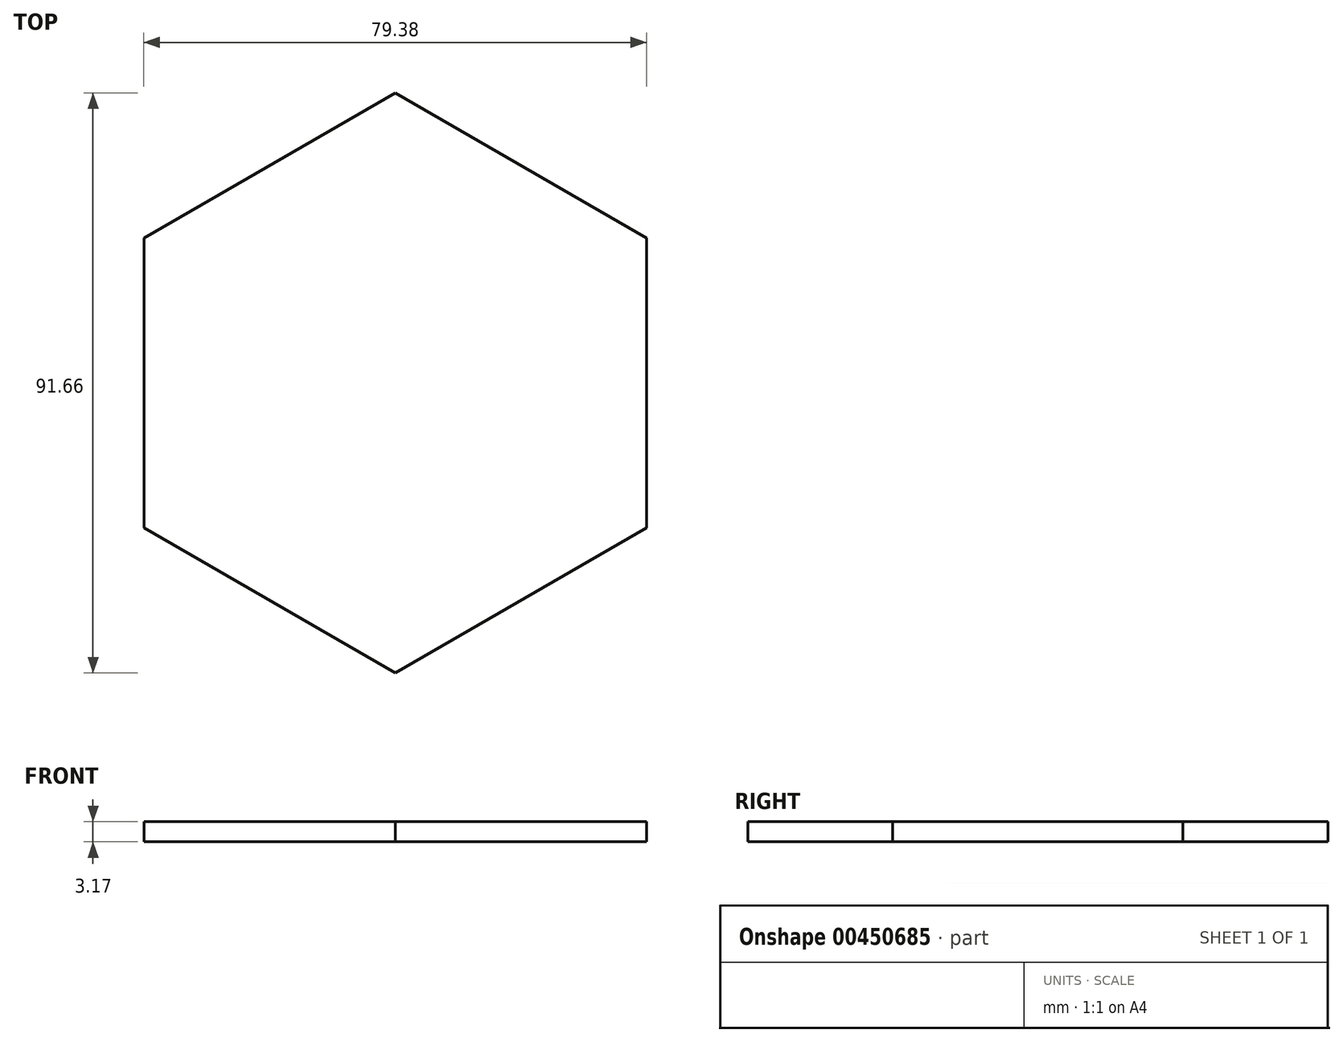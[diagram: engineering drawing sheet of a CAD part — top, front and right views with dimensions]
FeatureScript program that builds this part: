
annotation { "Feature Type Name" : "Feature", "Feature Type Description" : "" }
export const myFeature = defineFeature(function(context is Context, id is Id, definition is map)
    precondition{}
    {
        {
            var Q0;
            Q0=qCreatedBy(makeId("Top.planeOp"),FACE);
            var sketch = newSketch(context, id + "F0", { "sketchPlane" : qUnion([Q0])});
            skCircle(sketch, "E0.cCircle", {"center": v(0, 0) * mm, "radius": 39.69 * mm, "construction": true});
            skLineSegment(sketch, "E0.0", {"start": v(39.69, -22.91) * mm, "end": v(0, -45.83) * mm});
            skLineSegment(sketch, "E0.1", {"start": v(0, -45.83) * mm, "end": v(-39.69, -22.91) * mm});
            skLineSegment(sketch, "E0.2", {"start": v(-39.69, -22.91) * mm, "end": v(-39.69, 22.91) * mm});
            skLineSegment(sketch, "E0.3", {"start": v(-39.69, 22.91) * mm, "end": v(0, 45.83) * mm});
            skLineSegment(sketch, "E0.4", {"start": v(0, 45.83) * mm, "end": v(39.69, 22.91) * mm});
            skLineSegment(sketch, "E0.5", {"start": v(39.69, 22.91) * mm, "end": v(39.69, -22.91) * mm});
            skPoint(sketch, "E0.0.midPoint", {"position": v(19.84, -34.37) * mm});
            skSolve(sketch);
        }
        {
            var Q0;
            Q0 = qSketchRegion(id + "F0", true);
            extrude(context, id + "F1", {"entities" : qUnion([Q0]), "depth" : 3.17 * mm});
        }
    });
